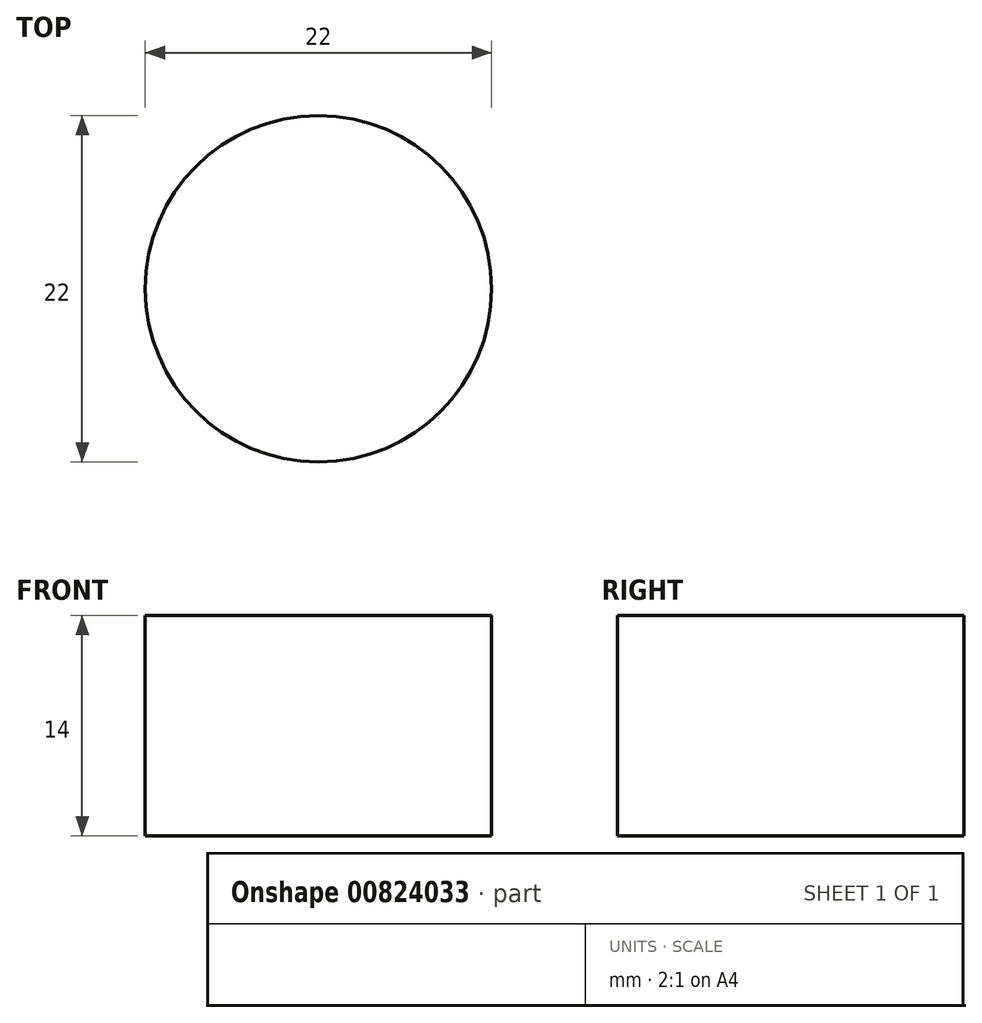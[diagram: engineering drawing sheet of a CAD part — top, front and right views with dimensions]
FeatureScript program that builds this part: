
annotation { "Feature Type Name" : "Feature", "Feature Type Description" : "" }
export const myFeature = defineFeature(function(context is Context, id is Id, definition is map)
    precondition{}
    {
        {
            var Q0;
            Q0=qCreatedBy(makeId("Top.planeOp"),FACE);
            var sketch = newSketch(context, id + "F0", { "sketchPlane" : qUnion([Q0])});
            skCircle(sketch, "E0", {"center": v(0, 0) * mm, "radius": 11 * mm});
            skSolve(sketch);
        }
        {
            var Q0;
            Q0=makeQuery(id+"F0.imprint","IMPRINT",FACE,{"disambiguationData":[TD([[makeQuery(id+"F0.imprint","IMPRINT",EDGE,{"derivedFrom":sQuery(id+"F0.wireOp",EDGE,"E0")}),1.0]])]});
            extrude(context, id + "F1", {"entities" : qUnion([Q0]), "depth" : 14 * mm, "offsetDistance" : 25 * mm});
        }
    });
